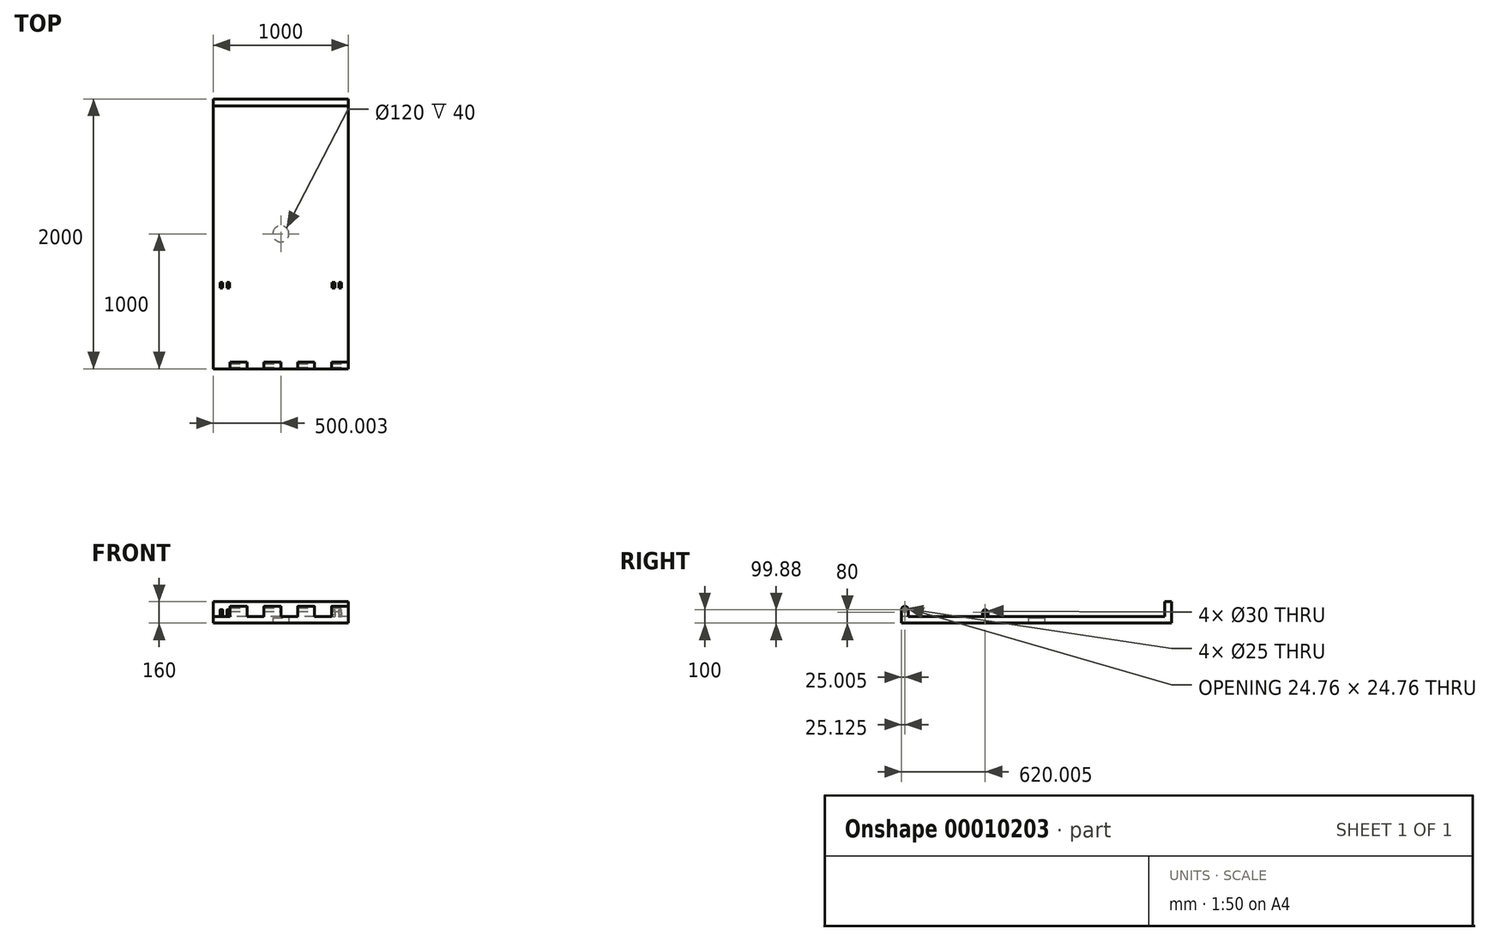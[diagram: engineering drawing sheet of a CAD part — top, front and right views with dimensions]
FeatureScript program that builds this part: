
annotation { "Feature Type Name" : "Feature", "Feature Type Description" : "" }
export const myFeature = defineFeature(function(context is Context, id is Id, definition is map)
    precondition{}
    {
        {
            var Q0;
            Q0=qCreatedBy(makeId("Top.planeOp"),FACE);
            var sketch = newSketch(context, id + "F0", { "sketchPlane" : qUnion([Q0])});
            skLineSegment(sketch, "E0.bottom", {"start": v(-409.07, -956.56) * mm, "end": v(590.93, -956.56) * mm});
            skLineSegment(sketch, "E0.top", {"start": v(-409.07, 1043.44) * mm, "end": v(590.93, 1043.44) * mm});
            skLineSegment(sketch, "E0.left", {"start": v(-409.07, -956.56) * mm, "end": v(-409.07, 1043.44) * mm});
            skLineSegment(sketch, "E0.right", {"start": v(590.93, -956.56) * mm, "end": v(590.93, 1043.44) * mm});
            skSolve(sketch);
        }
        {
            var Q0;
            Q0 = qSketchRegion(id + "F0", true);
            extrude(context, id + "F1", {"entities" : qUnion([Q0]), "depth" : 50 * mm});
        }
        {
            var Q0;
            Q0=makeQuery(id+"F1.opExtrude","SWEPT_FACE",FACE,{"disambiguationData":[OSD([sQuery(id+"F0.wireOp",EDGE,"E0.right")])]});
            var sketch = newSketch(context, id + "F2", { "sketchPlane" : qUnion([Q0])});
            skLineSegment(sketch, "E1.bottom", {"start": v(-956.56, 50) * mm, "end": v(-906.56, 50) * mm});
            skLineSegment(sketch, "E1.left", {"start": v(-956.56, 50) * mm, "end": v(-956.56, 100) * mm});
            skLineSegment(sketch, "E1.right", {"start": v(-906.56, 50) * mm, "end": v(-906.56, 100) * mm});
            skArc(sketch, "E2", {"start": v(-906.56, 100) * mm, "mid": v(-931.56, 125) * mm, "end": v(-956.56, 100) * mm});
            skCircle(sketch, "E3", {"center": v(-931.56, 100) * mm, "radius": 12.5 * mm});
            skSolve(sketch);
        }
        {
            var Q0;
            Q0 = qSketchRegion(id + "F2", true);
            extrude(context, id + "F3", {"entities" : qUnion([Q0]), "oppositeDirection" : true, "depth" : 1000 * mm});
        }
        {
            var Q0;
            Q0=makeQuery(id+"F1.opExtrude","CAP_FACE",FACE,{"disambiguationData":[OSD([sQuery(id+"F0.wireOp",EDGE,"E0.bottom"),sQuery(id+"F0.wireOp",EDGE,"E0.top"),sQuery(id+"F0.wireOp",EDGE,"E0.left"),sQuery(id+"F0.wireOp",EDGE,"E0.right")])],"isStart":false});
            var sketch = newSketch(context, id + "F4", { "sketchPlane" : qUnion([Q0])});
            skLineSegment(sketch, "E4.bottom", {"start": v(-159.07, -818.58) * mm, "end": v(-34.07, -818.58) * mm});
            skLineSegment(sketch, "E4.top", {"start": v(-159.07, -1033.47) * mm, "end": v(-34.07, -1033.47) * mm});
            skLineSegment(sketch, "E4.left", {"start": v(-159.07, -818.58) * mm, "end": v(-159.07, -1033.47) * mm});
            skLineSegment(sketch, "E4.right", {"start": v(-34.07, -818.58) * mm, "end": v(-34.07, -1033.47) * mm});
            skLineSegment(sketch, "E5.bottom", {"start": v(90.93, -816.35) * mm, "end": v(215.93, -816.35) * mm});
            skLineSegment(sketch, "E5.top", {"start": v(90.93, -1023.71) * mm, "end": v(215.93, -1023.71) * mm});
            skLineSegment(sketch, "E5.left", {"start": v(90.93, -816.35) * mm, "end": v(90.93, -1023.71) * mm});
            skLineSegment(sketch, "E5.right", {"start": v(215.93, -816.35) * mm, "end": v(215.93, -1023.71) * mm});
            skLineSegment(sketch, "E6.bottom", {"start": v(340.93, -840.14) * mm, "end": v(465.93, -840.14) * mm});
            skLineSegment(sketch, "E6.top", {"start": v(340.93, -1023.71) * mm, "end": v(465.93, -1023.71) * mm});
            skLineSegment(sketch, "E6.left", {"start": v(340.93, -840.14) * mm, "end": v(340.93, -1023.71) * mm});
            skLineSegment(sketch, "E6.right", {"start": v(465.93, -840.14) * mm, "end": v(465.93, -1023.71) * mm});
            skLineSegment(sketch, "E7.bottom", {"start": v(-284.07, -802.65) * mm, "end": v(-409.07, -802.65) * mm});
            skLineSegment(sketch, "E7.top", {"start": v(-284.07, -1062.3) * mm, "end": v(-409.07, -1062.3) * mm});
            skLineSegment(sketch, "E7.left", {"start": v(-284.07, -802.65) * mm, "end": v(-284.07, -1062.3) * mm});
            skLineSegment(sketch, "E7.right", {"start": v(-409.07, -802.65) * mm, "end": v(-409.07, -1062.3) * mm});
            skSolve(sketch);
        }
        {
            var Q0;
            Q0 = qSketchRegion(id + "F4", true);
            extrude(context, id + "F5", {"entities" : qUnion([Q0]), "operationType" : NewBodyOperationType.REMOVE, "endBound" : BoundingType.THROUGH_ALL, "depth" : 60 * mm});
        }
        {
            var Q0;
            Q0=makeQuery(id+"F1.opExtrude","SWEPT_BODY",BODY,{"disambiguationData":[OSD([sQuery(id+"F0.wireOp",EDGE,"E0.bottom"),sQuery(id+"F0.wireOp",EDGE,"E0.top"),sQuery(id+"F0.wireOp",EDGE,"E0.left"),sQuery(id+"F0.wireOp",EDGE,"E0.right")])]});
            var Q1;
            Q1=makeQuery(id+"F5.boolean.opBoolean","SPLIT",BODY,{"disambiguationData":[OD(0.0)],"derivedFrom":makeQuery(id+"F3.opExtrude","SWEPT_BODY",BODY,{"disambiguationData":[OSD([sQuery(id+"F2.wireOp",EDGE,"E1.bottom"),sQuery(id+"F2.wireOp",EDGE,"E1.left"),sQuery(id+"F2.wireOp",EDGE,"E1.right"),sQuery(id+"F2.wireOp",EDGE,"E2"),sQuery(id+"F2.wireOp",EDGE,"E3")])]})});
            var Q2;
            Q2=makeQuery(id+"F5.boolean.opBoolean","SPLIT",BODY,{"disambiguationData":[OD(1.0)],"derivedFrom":makeQuery(id+"F3.opExtrude","SWEPT_BODY",BODY,{"disambiguationData":[OSD([sQuery(id+"F2.wireOp",EDGE,"E1.bottom"),sQuery(id+"F2.wireOp",EDGE,"E1.left"),sQuery(id+"F2.wireOp",EDGE,"E1.right"),sQuery(id+"F2.wireOp",EDGE,"E2"),sQuery(id+"F2.wireOp",EDGE,"E3")])]})});
            var Q3;
            Q3=makeQuery(id+"F5.boolean.opBoolean","SPLIT",BODY,{"disambiguationData":[OD(2.0)],"derivedFrom":makeQuery(id+"F3.opExtrude","SWEPT_BODY",BODY,{"disambiguationData":[OSD([sQuery(id+"F2.wireOp",EDGE,"E1.bottom"),sQuery(id+"F2.wireOp",EDGE,"E1.left"),sQuery(id+"F2.wireOp",EDGE,"E1.right"),sQuery(id+"F2.wireOp",EDGE,"E2"),sQuery(id+"F2.wireOp",EDGE,"E3")])]})});
            booleanBodies(context, id + "F6", {"operationType" : BooleanOperationType.UNION, "tools" : qUnion([Q0, Q1, Q2, Q3])});
        }
        {
            var Q0;
            Q0=makeQuery(id+"F6.opBoolean","MERGE",FACE,{"derivedFrom":[makeQuery(id+"F1.opExtrude","SWEPT_FACE",FACE,{"disambiguationData":[OSD([sQuery(id+"F0.wireOp",EDGE,"E0.right")])]}),makeQuery(id+"F3.opExtrude","CAP_FACE",FACE,{"disambiguationData":[OSD([sQuery(id+"F2.wireOp",EDGE,"E1.bottom"),sQuery(id+"F2.wireOp",EDGE,"E1.left"),sQuery(id+"F2.wireOp",EDGE,"E1.right"),sQuery(id+"F2.wireOp",EDGE,"E2"),sQuery(id+"F2.wireOp",EDGE,"E3")])],"isStart":true})]});
            var sketch = newSketch(context, id + "F7", { "sketchPlane" : qUnion([Q0])});
            skLineSegment(sketch, "E8.bottom", {"start": v(-356.56, 50) * mm, "end": v(-316.56, 50) * mm});
            skLineSegment(sketch, "E8.left", {"start": v(-356.56, 50) * mm, "end": v(-356.56, 80) * mm});
            skLineSegment(sketch, "E8.right", {"start": v(-316.56, 50) * mm, "end": v(-316.56, 80) * mm});
            skArc(sketch, "E9", {"start": v(-316.56, 80) * mm, "mid": v(-336.56, 100) * mm, "end": v(-356.56, 80) * mm});
            skCircle(sketch, "E10", {"center": v(-336.56, 80) * mm, "radius": 15 * mm});
            skSolve(sketch);
        }
        {
            var Q0;
            Q0 = qSketchRegion(id + "F7", true);
            extrude(context, id + "F8", {"entities" : qUnion([Q0]), "oppositeDirection" : true, "depth" : 1000 * mm});
        }
        {
            var Q0;
            Q0=makeQuery(id+"F8.opExtrude","SWEPT_FACE",FACE,{"disambiguationData":[OSD([sQuery(id+"F7.wireOp",EDGE,"E8.bottom")])]});
            var sketch = newSketch(context, id + "F9", { "sketchPlane" : qUnion([Q0])});
            skLineSegment(sketch, "E11.bottom", {"start": v(590.93, 316.56) * mm, "end": v(540.93, 316.56) * mm});
            skLineSegment(sketch, "E11.top", {"start": v(590.93, 483.59) * mm, "end": v(540.93, 483.59) * mm});
            skLineSegment(sketch, "E11.left", {"start": v(590.93, 316.56) * mm, "end": v(590.93, 483.59) * mm});
            skLineSegment(sketch, "E11.right", {"start": v(540.93, 316.56) * mm, "end": v(540.93, 483.59) * mm});
            skLineSegment(sketch, "E12.bottom", {"start": v(520.93, 316.56) * mm, "end": v(490.93, 316.56) * mm});
            skLineSegment(sketch, "E12.top", {"start": v(520.93, 470.01) * mm, "end": v(490.93, 470.01) * mm});
            skLineSegment(sketch, "E12.left", {"start": v(520.93, 316.56) * mm, "end": v(520.93, 470.01) * mm});
            skLineSegment(sketch, "E12.right", {"start": v(490.93, 316.56) * mm, "end": v(490.93, 470.01) * mm});
            skLineSegment(sketch, "E13.bottom", {"start": v(470.93, 316.56) * mm, "end": v(-289.07, 316.56) * mm});
            skLineSegment(sketch, "E13.top", {"start": v(470.93, 356.56) * mm, "end": v(-289.07, 356.56) * mm});
            skLineSegment(sketch, "E13.left", {"start": v(470.93, 316.56) * mm, "end": v(470.93, 356.56) * mm});
            skLineSegment(sketch, "E13.right", {"start": v(-289.07, 316.56) * mm, "end": v(-289.07, 356.56) * mm});
            skLineSegment(sketch, "E14.bottom", {"start": v(-359.07, 316.56) * mm, "end": v(-409.07, 316.56) * mm});
            skLineSegment(sketch, "E14.top", {"start": v(-359.07, 702.74) * mm, "end": v(-409.07, 702.74) * mm});
            skLineSegment(sketch, "E14.left", {"start": v(-359.07, 316.56) * mm, "end": v(-359.07, 702.74) * mm});
            skLineSegment(sketch, "E14.right", {"start": v(-409.07, 316.56) * mm, "end": v(-409.07, 702.74) * mm});
            skLineSegment(sketch, "E15.bottom", {"start": v(-309.07, 316.56) * mm, "end": v(-339.07, 316.56) * mm});
            skLineSegment(sketch, "E15.top", {"start": v(-309.07, 532.37) * mm, "end": v(-339.07, 532.37) * mm});
            skLineSegment(sketch, "E15.left", {"start": v(-309.07, 316.56) * mm, "end": v(-309.07, 532.37) * mm});
            skLineSegment(sketch, "E15.right", {"start": v(-339.07, 316.56) * mm, "end": v(-339.07, 532.37) * mm});
            skSolve(sketch);
        }
        {
            var Q0;
            Q0 = qSketchRegion(id + "F9", true);
            extrude(context, id + "F10", {"entities" : qUnion([Q0]), "operationType" : NewBodyOperationType.REMOVE, "endBound" : BoundingType.THROUGH_ALL, "oppositeDirection" : true, "depth" : 25 * mm});
        }
        {
            var Q0;
            Q0=makeQuery(id+"F1.opExtrude","CAP_FACE",FACE,{"disambiguationData":[OSD([sQuery(id+"F0.wireOp",EDGE,"E0.bottom"),sQuery(id+"F0.wireOp",EDGE,"E0.top"),sQuery(id+"F0.wireOp",EDGE,"E0.left"),sQuery(id+"F0.wireOp",EDGE,"E0.right")])],"isStart":false});
            var sketch = newSketch(context, id + "F11", { "sketchPlane" : qUnion([Q0])});
            skLineSegment(sketch, "E16.bottom", {"start": v(590.93, 1043.44) * mm, "end": v(-409.07, 1043.44) * mm});
            skLineSegment(sketch, "E16.top", {"start": v(590.93, 993.44) * mm, "end": v(-409.07, 993.44) * mm});
            skLineSegment(sketch, "E16.left", {"start": v(590.93, 1043.44) * mm, "end": v(590.93, 993.44) * mm});
            skLineSegment(sketch, "E16.right", {"start": v(-409.07, 1043.44) * mm, "end": v(-409.07, 993.44) * mm});
            skSolve(sketch);
        }
        {
            var Q0;
            Q0 = qSketchRegion(id + "F11", true);
            extrude(context, id + "F12", {"entities" : qUnion([Q0]), "operationType" : NewBodyOperationType.ADD, "depth" : 110 * mm});
        }
        {
            var Q0;
            Q0=makeQuery(id+"F1.opExtrude","CAP_FACE",FACE,{"disambiguationData":[OSD([sQuery(id+"F0.wireOp",EDGE,"E0.bottom"),sQuery(id+"F0.wireOp",EDGE,"E0.top"),sQuery(id+"F0.wireOp",EDGE,"E0.left"),sQuery(id+"F0.wireOp",EDGE,"E0.right")])],"isStart":true});
            var sketch = newSketch(context, id + "F13", { "sketchPlane" : qUnion([Q0])});
            skCircle(sketch, "E17", {"center": v(90.93, -43.44) * mm, "radius": 60 * mm});
            skSolve(sketch);
        }
        {
            var Q0;
            Q0=makeQuery(id+"F13.imprint","IMPRINT",FACE,{"disambiguationData":[TD([[makeQuery(id+"F13.imprint","IMPRINT",EDGE,{"derivedFrom":sQuery(id+"F13.wireOp",EDGE,"E17")}),1.0]])]});
            extrude(context, id + "F14", {"entities" : qUnion([Q0]), "operationType" : NewBodyOperationType.REMOVE, "oppositeDirection" : true, "depth" : 40 * mm});
        }
    });
